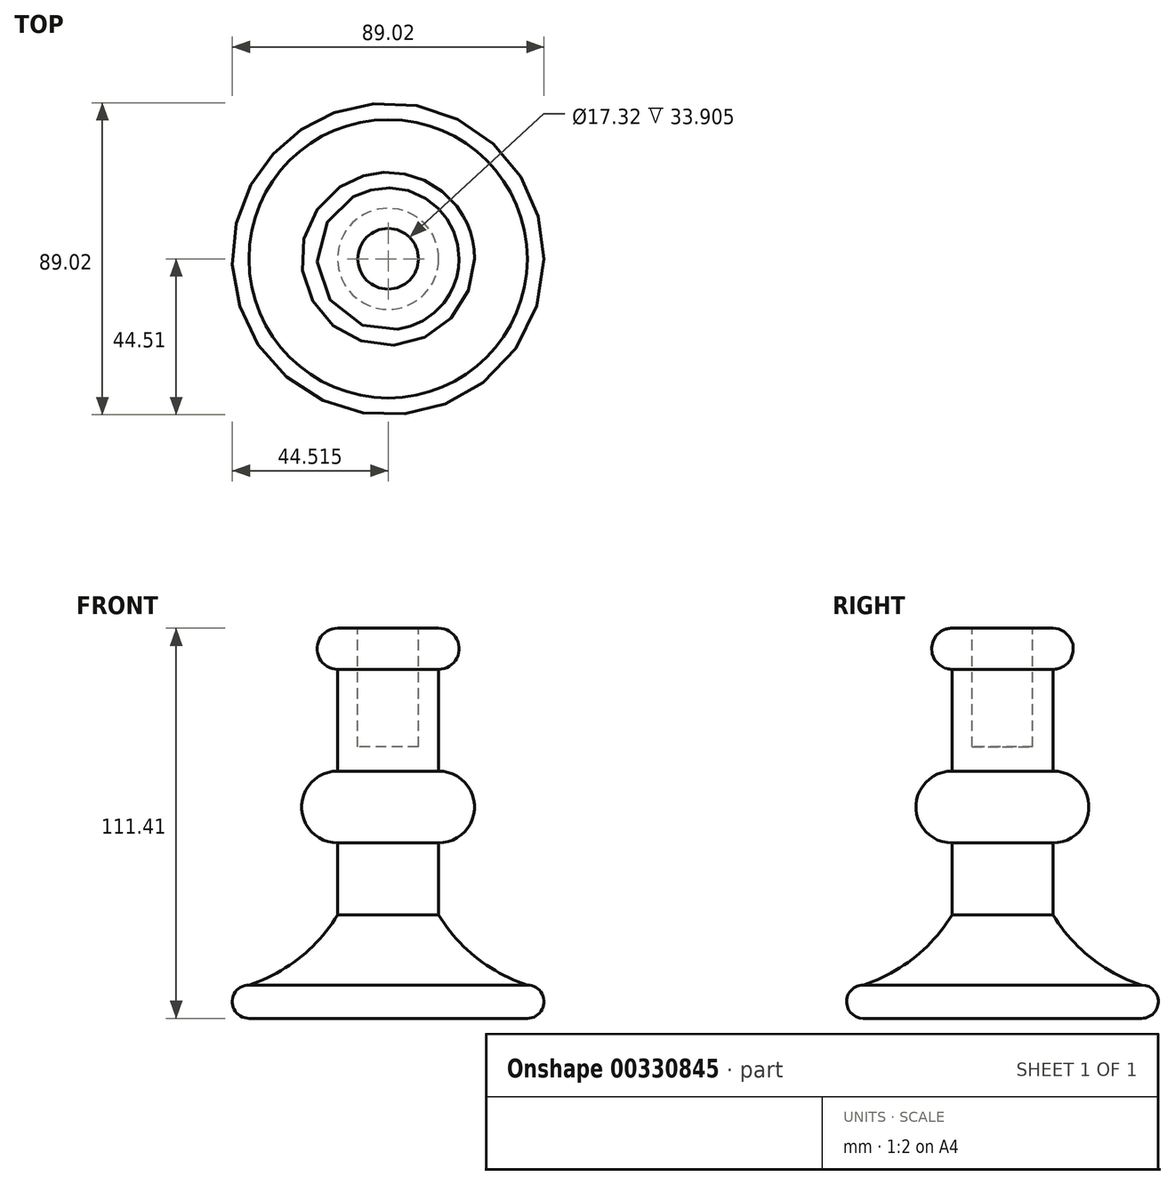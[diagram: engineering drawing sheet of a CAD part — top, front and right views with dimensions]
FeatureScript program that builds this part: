
annotation { "Feature Type Name" : "Feature", "Feature Type Description" : "" }
export const myFeature = defineFeature(function(context is Context, id is Id, definition is map)
    precondition{}
    {
        {
            var Q0;
            Q0=qCreatedBy(makeId("Front.planeOp"),FACE);
            var sketch = newSketch(context, id + "F0", { "sketchPlane" : qUnion([Q0])});
            skLineSegment(sketch, "E0", {"start": v(0, 0) * mm, "end": v(59.63, 0) * mm});
            skArc(sketch, "E1", {"start": v(59.63, 0) * mm, "mid": v(64.4, 4.77) * mm, "end": v(59.63, 9.53) * mm});
            skArc(sketch, "E2", {"start": v(34.31, 29.57) * mm, "mid": v(45.16, 17.26) * mm, "end": v(59.63, 9.53) * mm});
            skLineSegment(sketch, "E3", {"start": v(34.31, 29.57) * mm, "end": v(34.31, 50.09) * mm});
            skArc(sketch, "E4", {"start": v(34.31, 99.68) * mm, "mid": v(40.17, 105.55) * mm, "end": v(34.31, 111.41) * mm});
            skLineSegment(sketch, "E5", {"start": v(34.31, 111.41) * mm, "end": v(28.54, 111.41) * mm});
            skLineSegment(sketch, "E6", {"start": v(28.54, 111.41) * mm, "end": v(28.54, 77.5) * mm});
            skLineSegment(sketch, "E7", {"start": v(28.54, 77.5) * mm, "end": v(19.88, 77.5) * mm});
            skLineSegment(sketch, "E8", {"start": v(19.88, 77.5) * mm, "end": v(19.88, 0) * mm});
            skArc(sketch, "E9", {"start": v(34.31, 50.09) * mm, "mid": v(44.58, 60.36) * mm, "end": v(34.31, 70.63) * mm});
            skLineSegment(sketch, "E10.trimOffspring", {"start": v(34.31, 70.63) * mm, "end": v(34.31, 99.68) * mm});
            skSolve(sketch);
        }
        {
            var Q0;
            {var subQ1=sQuery(id+"F0.wireOp",EDGE,"E1");Q0=makeQuery(id+"F0.imprint","IMPRINT",FACE,{"disambiguationData":[TD([[makeQuery(id+"F0.imprint","IMPRINT",EDGE,{"derivedFrom":subQ1}),1.0]])]});}
            var Q1;
            Q1=sQuery(id+"F0.wireOp",EDGE,"E8");
            revolve(context, id + "F1", {"entities" : qUnion([Q0]), "axis" : qUnion([Q1]), "revolveType" : RevolveType.FULL});
        }
    });
